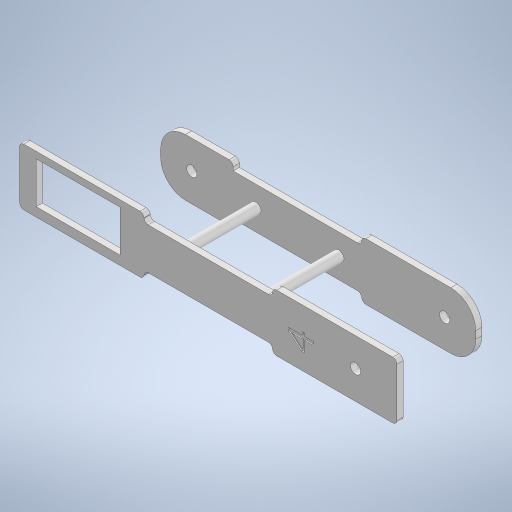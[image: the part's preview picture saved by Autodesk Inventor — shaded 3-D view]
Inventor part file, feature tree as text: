
AUTODESK INVENTOR PART (.ipt)
format: ipt  version: 2023 (Build 270158000, 158)  size: 381,952 bytes
history: native  units: mm
features: extrude x9, sketch x9, plane x2, other x1
ambient origin geometry x8: Origin, YZ Plane, XZ Plane, XY Plane, X Axis, Y Axis, Z Axis, Center Point
bodies: Body1 (feature_tree)
feature tree (21):
  other  "Sólido1"
  extrude  "Extrusión1"  Depth=60.0mm
  extrude  "Extrusión2"  Depth=20.0mm
  plane  "Plano de trabajo1"
  extrude  "Extrusión3"  Depth=27.5mm
  extrude  "Extrusión4"  Depth=3.0mm TaperAngle=0.0deg
  extrude  "Extrusión5"  Depth=5.0mm
  extrude  "Extrusión6"  Depth=3.0mm TaperAngle=0.0deg
  plane  "Plano de trabajo2"
  extrude  "Extrusión7"  Depth=27.5mm
  extrude  "Extrusión8"  Depth=152.0mm
  extrude  "Extrusión9"  Depth=62.0mm
  sketch  "Boceto1"  dims[d0=182.0mm d1=60.0mm]
  sketch  "Boceto2"  dims[d3=27.5mm d4=20.0mm]
  sketch  "Boceto3"  dims[d5=2.0mm d6=27.5mm]
  sketch  "Boceto4"  dims[d7=2.0mm d8=3.0mm d9=0.0mm]
  sketch  "Boceto5"  dims[d10=5.0mm d11=5.0mm]
  sketch  "Boceto6"  dims[d12=40.0mm d13=3.0mm d14=0.0mm]
  sketch  "Boceto7"  dims[d15=40.0mm d16=27.5mm]
  sketch  "Boceto8"  dims[d17=27.5mm d18=152.0mm]
  sketch  "Boceto9"  dims[d19=55.0mm d21=62.0mm d22=20.0mm d23=12.0mm d24=2.0mm d25=3.0mm d26=0.0mm d27=3.0mm d28=0.0mm d32=40.0mm d34=5.0mm d35=5.0mm d36=3.0mm d37=0.0mm d38=5.0mm d39=20.0mm d40=3.0mm d41=0.0mm d42=46.0mm d43=0.0mm d44=0.5mm d45=0.0mm d46=40.0mm d47=40.4mm d48=20.0mm d49=8.0mm d50=10.0mm d51=0.0mm]
